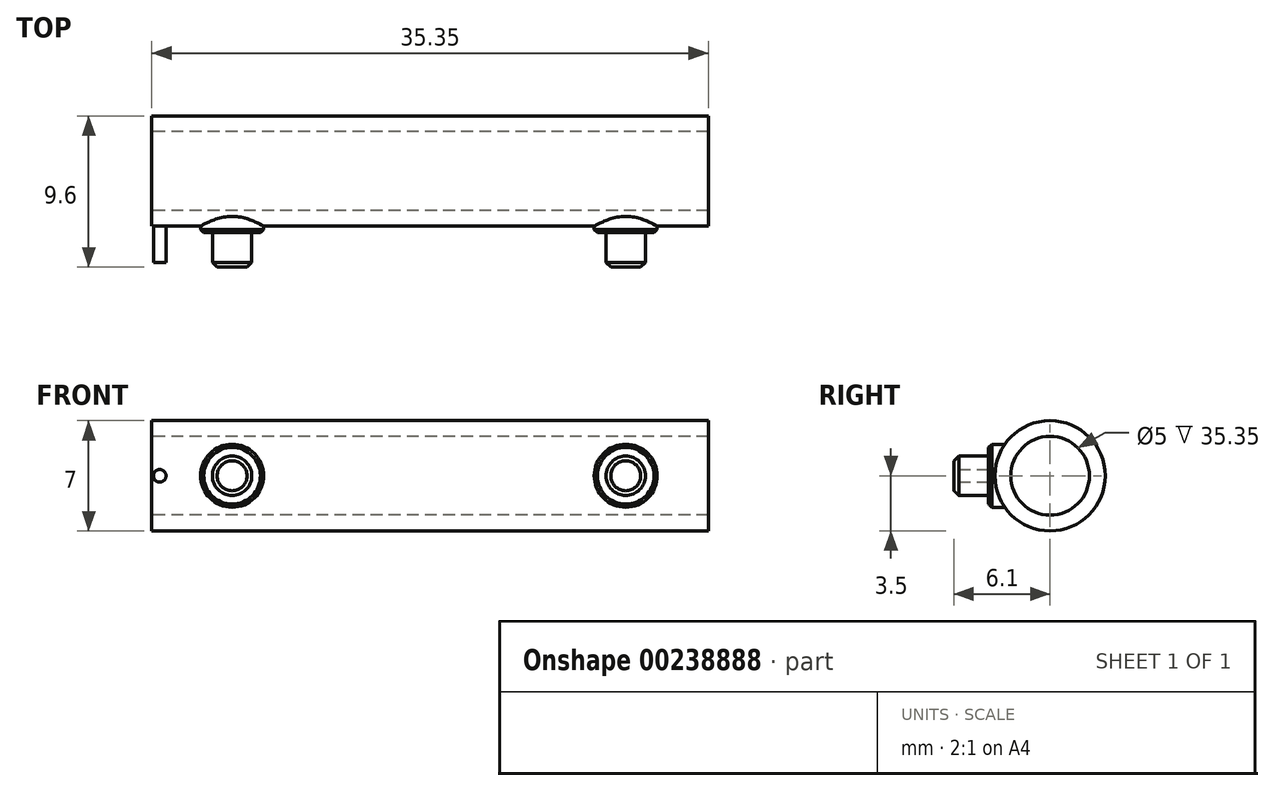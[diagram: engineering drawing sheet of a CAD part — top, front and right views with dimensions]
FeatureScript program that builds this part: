
annotation { "Feature Type Name" : "Feature", "Feature Type Description" : "" }
export const myFeature = defineFeature(function(context is Context, id is Id, definition is map)
    precondition{}
    {
        {
            var Q0;
            Q0=qCreatedBy(makeId("Right.planeOp"),FACE);
            var sketch = newSketch(context, id + "F0", { "sketchPlane" : qUnion([Q0])});
            skCircle(sketch, "E0", {"center": v(0, 0) * mm, "radius": 3.5 * mm});
            skCircle(sketch, "E1", {"center": v(0, 0) * mm, "radius": 2.5 * mm});
            skSolve(sketch);
        }
        {
            var Q0;
            Q0=makeQuery(id+"F0.imprint","IMPRINT",FACE,{"disambiguationData":[TD([[makeQuery(id+"F0.imprint","IMPRINT",EDGE,{"derivedFrom":sQuery(id+"F0.wireOp",EDGE,"E0")}),1.0]])]});
            extrude(context, id + "F1", {"entities" : qUnion([Q0]), "depth" : (35.35 - 0.8) * mm});
        }
        {
            var Q0;
            Q0=qCreatedBy(makeId("Right.planeOp"),FACE);
            cPlane(context, id + "F2", {"entities" : qUnion([Q0]), "cplaneType" : CPlaneType.OFFSET, "offset" : 0 * mm, "width" : 150 * mm, "height" : 150 * mm});
        }
        {
            var Q0;
            Q0=qCreatedBy(id+"F2.planeOp",FACE);
            var sketch = newSketch(context, id + "F3", { "sketchPlane" : qUnion([Q0])});
            skLineSegment(sketch, "E2", {"start": v(-3.5, 0) * mm, "end": v(-6.1, 0) * mm});
            skSolve(sketch);
        }
        {
            var Q0;
            Q0=qCreatedBy(makeId("Front.planeOp"),FACE);
            var Q1;
            Q1=sQuery(id+"F3.wireOp",VERTEX,"E2.start");
            cPlane(context, id + "F4", {"entities" : qUnion([Q0, Q1]), "cplaneType" : CPlaneType.PLANE_POINT, "offset" : 25 * mm, "width" : 150 * mm, "height" : 150 * mm});
        }
        {
            var Q0;
            Q0=qCreatedBy(id+"F4.planeOp",FACE);
            var sketch = newSketch(context, id + "F5", { "sketchPlane" : qUnion([Q0])});
            skCircle(sketch, "E3", {"center": v(0.1, 0) * mm, "radius": 0.4 * mm});
            skLineSegment(sketch, "E4", {"start": v(0, 0) * mm, "end": v(0.1, 0) * mm, "construction": true});
            skSolve(sketch);
        }
        {
            var Q0;
            Q0=makeQuery(id+"F1.opExtrude","CAP_FACE",FACE,{"disambiguationData":[OSD([sQuery(id+"F0.wireOp",EDGE,"E0"),sQuery(id+"F0.wireOp",EDGE,"E1")])],"isStart":true});
            extrude(context, id + "F6", {"entities" : qUnion([Q0]), "operationType" : NewBodyOperationType.ADD, "depth" : 0.4 * mm});
        }
        {
            var Q0;
            Q0=makeQuery(id+"F1.opExtrude","CAP_FACE",FACE,{"disambiguationData":[OSD([sQuery(id+"F0.wireOp",EDGE,"E0"),sQuery(id+"F0.wireOp",EDGE,"E1")])],"isStart":false});
            extrude(context, id + "F7", {"entities" : qUnion([Q0]), "operationType" : NewBodyOperationType.ADD, "depth" : 0.4 * mm});
        }
        {
            var Q0;
            Q0=qCreatedBy(makeId("Front.planeOp"),FACE);
            var Q1;
            Q1=sQuery(id+"F5.wireOp",VERTEX,"E3.center");
            cPlane(context, id + "F8", {"entities" : qUnion([Q0, Q1]), "cplaneType" : CPlaneType.PLANE_POINT, "offset" : 25 * mm, "width" : 150 * mm, "height" : 150 * mm});
        }
        {
            var Q0;
            Q0=qCreatedBy(id+"F8.planeOp",FACE);
            var sketch = newSketch(context, id + "F9", { "sketchPlane" : qUnion([Q0])});
            skCircle(sketch, "E5", {"center": v(4.7, 0) * mm, "radius": 2 * mm});
            skCircle(sketch, "E6", {"center": v(29.7, 0) * mm, "radius": 2 * mm});
            skSolve(sketch);
        }
        {
            var Q0;
            Q0=qSketchRegion(id+"F9",true);
            extrude(context, id + "F10", {"entities" : qUnion([Q0]), "operationType" : NewBodyOperationType.ADD, "depth" : 0.4 * mm, "hasSecondDirection" : true, "secondDirectionOppositeDirection" : true, "secondDirectionDepth" : 1 * mm});
        }
        {
            var Q0;
            Q0=makeQuery(id+"F10.opExtrude","CAP_FACE",FACE,{"disambiguationData":[OSD([sQuery(id+"F9.wireOp",EDGE,"E5")])],"isStart":false});
            var sketch = newSketch(context, id + "F11", { "sketchPlane" : qUnion([Q0])});
            skCircle(sketch, "E7", {"center": v(4.7, 0) * mm, "radius": 1.25 * mm});
            skCircle(sketch, "E8", {"center": v(29.7, 0) * mm, "radius": 1.25 * mm});
            skSolve(sketch);
        }
        {
            var Q0;
            Q0=makeQuery(id+"F11.imprint","IMPRINT",FACE,{"disambiguationData":[TD([[makeQuery(id+"F11.imprint","IMPRINT",EDGE,{"derivedFrom":sQuery(id+"F11.wireOp",EDGE,"E7")}),1.0]])]});
            var Q1;
            Q1=makeQuery(id+"F11.imprint","IMPRINT",FACE,{"disambiguationData":[TD([[makeQuery(id+"F11.imprint","IMPRINT",EDGE,{"derivedFrom":sQuery(id+"F11.wireOp",EDGE,"E8")}),1.0]])]});
            extrude(context, id + "F12", {"entities" : qUnion([Q0, Q1]), "operationType" : NewBodyOperationType.ADD, "depth" : (2.6 - 0.4) * mm});
        }
        {
            var Q0;
            Q0=makeQuery(id+"F10.opExtrude","CAP_EDGE",EDGE,{"disambiguationData":[OSD([sQuery(id+"F9.wireOp",EDGE,"E5")])],"isStart":false});
            var Q1;
            Q1=makeQuery(id+"F10.opExtrude","CAP_EDGE",EDGE,{"disambiguationData":[OSD([sQuery(id+"F9.wireOp",EDGE,"E6")])],"isStart":false});
            chamfer(context, id + "F13", {"entities" : qUnion([Q0, Q1]), "width" : 0.2 * mm, "tangentPropagation" : true});
        }
        {
            var Q0;
            Q0=makeQuery(id+"F12.opExtrude","CAP_EDGE",EDGE,{"disambiguationData":[OSD([sQuery(id+"F11.wireOp",EDGE,"E7")])],"isStart":false});
            var Q1;
            Q1=makeQuery(id+"F12.opExtrude","CAP_EDGE",EDGE,{"disambiguationData":[OSD([sQuery(id+"F11.wireOp",EDGE,"E8")])],"isStart":false});
            chamfer(context, id + "F14", {"entities" : qUnion([Q0, Q1]), "width" : 0.3 * mm, "tangentPropagation" : true});
        }
        {
            var Q0;
            Q0=makeQuery(id+"F5.imprint","IMPRINT",FACE,{"disambiguationData":[TD([[makeQuery(id+"F5.imprint","IMPRINT",EDGE,{"derivedFrom":sQuery(id+"F5.wireOp",EDGE,"E3")}),1.0]])]});
            extrude(context, id + "F15", {"entities" : qUnion([Q0]), "depth" : (9.6 - 7.3) * mm});
        }
    });
